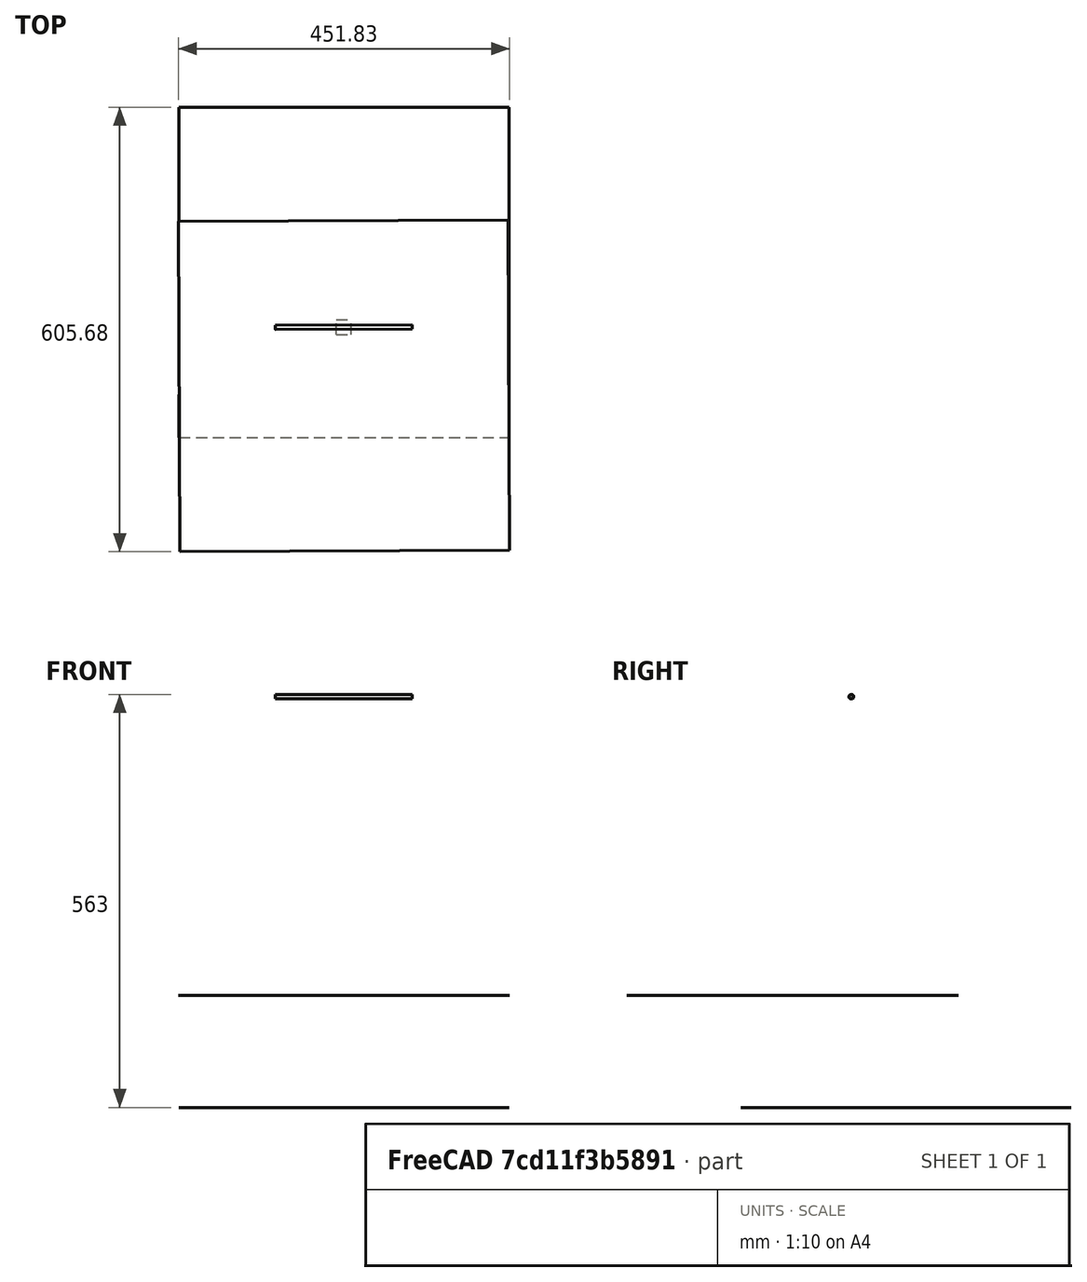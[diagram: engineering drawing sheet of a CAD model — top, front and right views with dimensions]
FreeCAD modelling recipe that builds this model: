
FCSTD DOCUMENT  (FreeCAD 0.19R18044 (Git))
Label: lift
License: Public Domain
LicenseURL: http://en.wikipedia.org/wiki/Public_domain
objects: App::FeaturePython×12, Part::FeaturePython×11, App::Link×2
note: 10 computed .brp shape members not serialized (recipe doc carries the construction recipe); baked Part::Feature solids carry a one-line shape summary decoded from their .brp
EXTERNAL_REF file=lift-middle-stage.FCStd obj=Assembly002
EXTERNAL_REF file=lift-upper-stage.FCStd obj=Assembly

FEATURE [App::Link] Link  label="lift-middle-stage"
  LinkPlacement = pos=(-0.373772,-74.7387,8.54139e-05) rot=(0,0,1;0.004077rad)
  LinkedObject = -> <external lift-middle-stage.FCStd>#Assembly002
  Placement = pos=(-0.373772,-74.7387,8.54139e-05) rot=(0,0,1;0.004077rad)
FEATURE [App::Link] Link001  label="lift-upper-stage"
  LinkPlacement = pos=(-0.0475156,-154.766,153) rot=(0,0,1;0.004077rad)
  LinkedObject = -> <external lift-upper-stage.FCStd>#Assembly
  Placement = pos=(-0.0475156,-154.766,153) rot=(0,0,1;0.004077rad)
FEATURE [Part::FeaturePython] Parts  # WARN: FeaturePython — macro-defined, semantics opaque (R4)
  Group = -> [Link,Link001,Origin]
  GroupMode = 0
FEATURE [Part::FeaturePython] Assembly  label="lift"  # WARN: FeaturePython — macro-defined, semantics opaque (R4)
  AutoRelax = true
  BuildShape = 0
  Freeze = false
  Group = -> [Constraints,Elements,Parts]
  GroupMode = 1
  SolverType = 1
  Verbose = false
  _SolverType = 1
  _Version = 1
FEATURE [App::FeaturePython] Constraints  # WARN: FeaturePython — macro-defined, semantics opaque (R4)
  Group = -> [Constraint,Constraint001,Constraint002]
  GroupMode = 1
  _Version = 1
FEATURE [App::FeaturePython] Elements  # WARN: FeaturePython — macro-defined, semantics opaque (R4)
  Group = -> [_Element,_Element001,_Element002,_Element003,_Element004,_Element005,_Element006,_Element007,_Element008]
  GroupMode = 1
FEATURE [App::FeaturePython] Constraint  label="MultiParallel"  # WARN: FeaturePython — macro-defined, semantics opaque (R4)
  Angle = 0
  AnglePitch = 0
  AngleRoll = 0
  ConstraintType = 6
  Disabled = false
  Group = -> [ElementLink,ElementLink001,ElementLink002]
  GroupMode = 1
  LockAngle = false
  _ConstraintType = 291
  _Parent = -> Constraints
FEATURE [App::FeaturePython] ElementLink  label="_Element"  # link proxy (typed FeaturePython)
  LinkTransform = true
  LinkedObject = -> _Element
  _Parent = -> Constraint
FEATURE [Part::FeaturePython] _Element  # link proxy (typed FeaturePython)
  Detach = false
  LinkTransform = true
  LinkedObject = -> Link [1.$_Element026.]
  _Parent = -> Elements
FEATURE [App::FeaturePython] ElementLink001  label="_Element001"  # link proxy (typed FeaturePython)
  LinkTransform = true
  LinkedObject = -> _Element001
  _Parent = -> Constraint
FEATURE [Part::FeaturePython] _Element001  # link proxy (typed FeaturePython)
  Detach = false
  LinkTransform = true
  LinkedObject = -> Link001 [1.$_Element024.]
  _Parent = -> Elements
FEATURE [App::FeaturePython] ElementLink002  label="_Element002"  # link proxy (typed FeaturePython)
  LinkTransform = true
  LinkedObject = -> _Element002
  _Parent = -> Constraint
FEATURE [Part::FeaturePython] _Element002  # link proxy (typed FeaturePython)
  Detach = false
  LinkTransform = true
  LinkedObject = -> Origin [XY_Plane.]
  _Parent = -> Elements
FEATURE [App::FeaturePython] Constraint001  label="AxialAlignment"  # WARN: FeaturePython — macro-defined, semantics opaque (R4)
  Angle = 0
  AnglePitch = 0
  AngleRoll = 0
  ConstraintType = 4
  Disabled = false
  Group = -> [ElementLink003,ElementLink004]
  GroupMode = 1
  LockAngle = false
  Multiply = false
  _ConstraintType = 36
  _Parent = -> Constraints
FEATURE [App::FeaturePython] ElementLink003  label="_Element003"  # link proxy (typed FeaturePython)
  LinkTransform = true
  LinkedObject = -> _Element003
  _Parent = -> Constraint001
FEATURE [Part::FeaturePython] _Element003  # link proxy (typed FeaturePython)
  Detach = false
  LinkTransform = true
  LinkedObject = -> Link001 [1.$Element.]
  _Parent = -> Elements
FEATURE [App::FeaturePython] ElementLink004  label="_Element004"  # link proxy (typed FeaturePython)
  LinkTransform = true
  LinkedObject = -> _Element004
  _Parent = -> Constraint001
FEATURE [Part::FeaturePython] _Element004  # link proxy (typed FeaturePython)
  Detach = false
  LinkTransform = true
  LinkedObject = -> Link [1.$Element002.]
  _Parent = -> Elements
FEATURE [Part::FeaturePython] _Element005  # link proxy (typed FeaturePython)
  Detach = false
  LinkTransform = true
  LinkedObject = -> Link001 [1.$Element001.]
  _Parent = -> Elements
FEATURE [Part::FeaturePython] _Element006  # link proxy (typed FeaturePython)
  Detach = false
  LinkTransform = true
  LinkedObject = -> Link [1.$_Element.]
  _Parent = -> Elements
FEATURE [Part::FeaturePython] _Element007  # link proxy (typed FeaturePython)
  Detach = false
  LinkTransform = true
  LinkedObject = -> Link [1.$Element003.]
  _Parent = -> Elements
FEATURE [Part::FeaturePython] _Element008  # link proxy (typed FeaturePython)
  Detach = false
  LinkTransform = true
  LinkedObject = -> Link [1.$Element004.]
  _Parent = -> Elements
FEATURE [App::FeaturePython] Constraint002  label="AxialAlignment001"  # WARN: FeaturePython — macro-defined, semantics opaque (R4)
  Angle = 0
  AnglePitch = 0
  AngleRoll = 0
  ConstraintType = 4
  Disabled = false
  Group = -> [ElementLink005,ElementLink006]
  GroupMode = 1
  LockAngle = false
  Multiply = false
  _ConstraintType = 36
  _Parent = -> Constraints
FEATURE [App::FeaturePython] ElementLink005  label="_Element007"  # link proxy (typed FeaturePython)
  LinkTransform = true
  LinkedObject = -> _Element007
  _Parent = -> Constraint002
FEATURE [App::FeaturePython] ElementLink006  label="_Element005"  # link proxy (typed FeaturePython)
  LinkTransform = true
  LinkedObject = -> _Element005
  _Parent = -> Constraint002

RESOLVED EXTERNAL PARTS (link-assembly join: the EXTERNAL_REF files above that resolve inside this repo's crawl, each included once):
---- part lift-middle-stage.FCStd = doc fcstd_024ec45ee0a4 ----
FCSTD DOCUMENT  (FreeCAD 0.19R18044 (Git))
Label: lift-middle-stage
License: Public Domain
LicenseURL: http://en.wikipedia.org/wiki/Public_domain
objects: App::FeaturePython×44, Part::FeaturePython×34, App::Link×6, App::LinkElement×4
note: 33 computed .brp shape members not serialized (recipe doc carries the construction recipe); baked Part::Feature solids carry a one-line shape summary decoded from their .brp
EXTERNAL_REF file=../parts/lift/middle-stage-actuator-rod.FCStd obj=Assembly
EXTERNAL_REF file=../parts/lift/middle-stage-beam.FCStd obj=Assembly001
EXTERNAL_REF file=../parts/lift/middle-stage-beam.FCStd obj=Assembly
EXTERNAL_REF file=../parts/common/linear-actuator-400.FCStd obj=Assembly004
EXTERNAL_REF file=../parts/common/rail-450.FCStd obj=Assembly002
EXTERNAL_REF file=../parts/common/rail-450.FCStd obj=Assembly

FEATURE [App::Link] Link  label="middle-stage-actuator-rod"
  LinkPlacement = pos=(0,-6.67572e-05,560) rot=(0,0,1;0rad)
  LinkedObject = -> <external ../parts/lift/middle-stage-actuator-rod.FCStd>#Assembly
  Placement = pos=(0,-6.67572e-05,560) rot=(0,0,1;0rad)
FEATURE [App::Link] Link001  label="middle-stage-beam-left"
  LinkPlacement = pos=(71.3,-24.5001,10.0001) rot=(0,0,1;0rad)
  LinkedObject = -> <external ../parts/lift/middle-stage-beam.FCStd>#Assembly001
  Placement = pos=(71.3,-24.5001,10.0001) rot=(0,0,1;0rad)
FEATURE [App::Link] Link002  label="middle-stage-beam-right"
  LinkPlacement = pos=(49.7,-24.5001,10.0001) rot=(0,0,1;0rad)
  LinkedObject = -> <external ../parts/lift/middle-stage-beam.FCStd>#Assembly
  Placement = pos=(49.7,-24.5001,10.0001) rot=(0,0,1;0rad)
FEATURE [App::Link] Link003  label="actuator_a"
  LinkPlacement = pos=(7.1213e-12,-6.67572e-05,44.0001) rot=(0,0,1;3.14159rad)
  LinkedObject = -> <external ../parts/common/linear-actuator-400.FCStd>#Assembly004
  Placement = pos=(7.1213e-12,-6.67572e-05,44.0001) rot=(0,0,1;3.14159rad)
FEATURE [App::LinkElement] Link004_i0  label="left"
  LinkPlacement = pos=(106,-6.67572e-05,565) rot=(0.57735,-0.57735,-0.57735;2.0944rad)
  LinkedObject = -> <external ../parts/common/rail-450.FCStd>#Assembly002
  Placement = pos=(106,-6.67572e-05,565) rot=(0.57735,-0.57735,-0.57735;2.0944rad)
FEATURE [App::LinkElement] Link004_i1  label="right"
  LinkPlacement = pos=(-106,-6.67572e-05,565) rot=(0.57735,0.57735,0.57735;2.0944rad)
  LinkedObject = -> <external ../parts/common/rail-450.FCStd>#Assembly002
  Placement = pos=(-106,-6.67572e-05,565) rot=(0.57735,0.57735,0.57735;2.0944rad)
FEATURE [App::Link] Link004  label="rail top"
  ElementCount = 2
  ElementList = -> [Link004_i0,Link004_i1]
  LinkedObject = -> <external ../parts/common/rail-450.FCStd>#Assembly002
FEATURE [App::LinkElement] Link005_i0  label="rail-upper-left"
  LinkPlacement = pos=(93.3,-49.0001,610) rot=(0.57735,0.57735,0.57735;2.0944rad)
  LinkedObject = -> <external ../parts/common/rail-450.FCStd>#Assembly
  Placement = pos=(93.3,-49.0001,610) rot=(0.57735,0.57735,0.57735;2.0944rad)
FEATURE [App::LinkElement] Link005_i1  label="rail-upper-right"
  LinkPlacement = pos=(-93.3,-49.0001,610) rot=(0.57735,-0.57735,-0.57735;2.0944rad)
  LinkedObject = -> <external ../parts/common/rail-450.FCStd>#Assembly
  Placement = pos=(-93.3,-49.0001,610) rot=(0.57735,-0.57735,-0.57735;2.0944rad)
FEATURE [App::Link] Link005  label="rail bottom"
  ElementCount = 2
  ElementList = -> [Link005_i0,Link005_i1]
  LinkedObject = -> <external ../parts/common/rail-450.FCStd>#Assembly
FEATURE [Part::FeaturePython] Parts002  label="Parts"  # WARN: FeaturePython — macro-defined, semantics opaque (R4)
  Group = -> [Origin004,Link,Link001,Link002,Link003,Link004,Link005]
  GroupMode = 0
FEATURE [Part::FeaturePython] Assembly002  label="lift-middle-stage"  # WARN: FeaturePython — macro-defined, semantics opaque (R4)
  AutoRelax = true
  BuildShape = 0
  Freeze = false
  Group = -> [Constraints002,Elements002,Parts002]
  GroupMode = 1
  SolverType = 1
  Verbose = false
  _SolverType = 1
  _Version = 1
FEATURE [App::FeaturePython] Constraints002  # WARN: FeaturePython — macro-defined, semantics opaque (R4)
  Group = -> [Constraint,Constraint003,Constraint004,Constraint005,Constraint006,Constraint007,Constraint008,Constraint009,Constraint010,Constraint011,Constraint012,Constraint013,Constraint014,Constraint015]
  GroupMode = 1
  _Version = 1
FEATURE [App::FeaturePython] Elements002  label="Elements"  # WARN: FeaturePython — macro-defined, semantics opaque (R4)
  Group = -> [_Element,_Element001,_Element002,_Element003,_Element004,_Element005,_Element006,_Element007,_Element008,_Element009,_Element010,_Element011,_Element012,_Element013,_Element014,_Element015,_Element016,_Element017,_Element018,_Element019,_Element020,_Element021,_Element022,_Element023,_Element024,Element,Element001,_Element025,_Element026,Element002,Element003,Element004]
  GroupMode = 1
FEATURE [App::FeaturePython] Constraint  label="Locked"  # WARN: FeaturePython — macro-defined, semantics opaque (R4)
  ConstraintType = 0
  Disabled = false
  Group = -> [ElementLink]
  GroupMode = 1
  _ConstraintType = 0
  _Parent = -> Constraints002
FEATURE [App::FeaturePython] ElementLink  label="_Element"  # link proxy (typed FeaturePython)
  LinkTransform = true
  LinkedObject = -> _Element
  _Parent = -> Constraint
FEATURE [Part::FeaturePython] _Element  # link proxy (typed FeaturePython)
  Detach = false
  LinkTransform = true
  LinkedObject = -> Link [1.$Element003.]
  _Parent = -> Elements002
FEATURE [Part::FeaturePython] _Element001  # link proxy (typed FeaturePython)
  Detach = false
  LinkTransform = true
  LinkedObject = -> Link001 [1.$actuator-rod-hole.]
  _Parent = -> Elements002
FEATURE [Part::FeaturePython] _Element002  # link proxy (typed FeaturePython)
  Detach = false
  LinkTransform = true
  LinkedObject = -> Link [1.$left.]
  _Parent = -> Elements002
FEATURE [Part::FeaturePython] _Element003  # link proxy (typed FeaturePython)
  Detach = false
  LinkTransform = true
  LinkedObject = -> Link002 [1.$actuator_rod_hole.]
  _Parent = -> Elements002
FEATURE [Part::FeaturePython] _Element004  # link proxy (typed FeaturePython)
  Detach = false
  LinkTransform = true
  LinkedObject = -> Link [1.$right.]
  _Parent = -> Elements002
FEATURE [App::FeaturePython] Constraint003  label="PlaneCoincident002"  # WARN: FeaturePython — macro-defined, semantics opaque (R4)
  Angle = 0
  AnglePitch = 0
  AngleRoll = 0
  Cascade = false
  ConstraintType = 2
  Disabled = false
  Group = -> [ElementLink005,ElementLink006]
  GroupMode = 1
  LockAngle = false
  Multiply = false
  OffsetX = 0
  OffsetY = 0
  _ConstraintType = 35
  _Parent = -> Constraints002
FEATURE [App::FeaturePython] ElementLink005  label="_Element005"  # link proxy (typed FeaturePython)
  LinkTransform = true
  LinkedObject = -> _Element005
  _Parent = -> Constraint003
FEATURE [Part::FeaturePython] _Element005  # link proxy (typed FeaturePython)
  Detach = false
  LinkTransform = true
  LinkedObject = -> Link [1.$center.]
  _Parent = -> Elements002
FEATURE [App::FeaturePython] ElementLink006  label="_Element006"  # link proxy (typed FeaturePython)
  LinkTransform = true
  LinkedObject = -> _Element006
  _Parent = -> Constraint003
FEATURE [Part::FeaturePython] _Element006  # link proxy (typed FeaturePython)
  Detach = false
  LinkTransform = true
  LinkedObject = -> Link003 [1.$mount_top.]
  _Parent = -> Elements002
FEATURE [App::FeaturePython] Constraint004  label="PlaneCoincident003"  # WARN: FeaturePython — macro-defined, semantics opaque (R4)
  Angle = 0
  AnglePitch = 0
  AngleRoll = 0
  Cascade = false
  ConstraintType = 2
  Disabled = false
  Group = -> [ElementLink007,ElementLink008]
  GroupMode = 1
  LockAngle = false
  Multiply = false
  Offset = 1
  OffsetX = 0
  OffsetY = 0
  _ConstraintType = 35
  _Parent = -> Constraints002
FEATURE [App::FeaturePython] ElementLink007  label="_Element007"  # link proxy (typed FeaturePython)
  LinkTransform = true
  LinkedObject = -> _Element007
  _Parent = -> Constraint004
FEATURE [Part::FeaturePython] _Element007  # link proxy (typed FeaturePython)
  Detach = false
  LinkTransform = true
  LinkedObject = -> Link005 [Link005_i0.1.$mount_top.]
  _Parent = -> Elements002
FEATURE [App::FeaturePython] ElementLink008  label="_Element008"  # link proxy (typed FeaturePython)
  LinkTransform = true
  LinkedObject = -> _Element008
  _Parent = -> Constraint004
FEATURE [Part::FeaturePython] _Element008  # link proxy (typed FeaturePython)
  Detach = false
  LinkTransform = true
  LinkedObject = -> Link001 [1.$rail_upper_top.]
  _Parent = -> Elements002
FEATURE [App::FeaturePython] Constraint005  label="PlaneCoincident004"  # WARN: FeaturePython — macro-defined, semantics opaque (R4)
  Angle = 0
  AnglePitch = 0
  AngleRoll = 0
  Cascade = false
  ConstraintType = 2
  Disabled = false
  Group = -> [ElementLink009,ElementLink010]
  GroupMode = 1
  LockAngle = false
  Multiply = false
  Offset = 1
  OffsetX = 0
  OffsetY = 0
  _ConstraintType = 35
  _Parent = -> Constraints002
FEATURE [App::FeaturePython] ElementLink009  label="_Element009"  # link proxy (typed FeaturePython)
  LinkTransform = true
  LinkedObject = -> _Element009
  _Parent = -> Constraint005
FEATURE [Part::FeaturePython] _Element009  # link proxy (typed FeaturePython)
  Detach = false
  LinkTransform = true
  LinkedObject = -> Link001 [1.$rail_upper_bottom.]
  _Parent = -> Elements002
FEATURE [App::FeaturePython] ElementLink010  label="_Element010"  # link proxy (typed FeaturePython)
  LinkTransform = true
  LinkedObject = -> _Element010
  _Parent = -> Constraint005
FEATURE [Part::FeaturePython] _Element010  # link proxy (typed FeaturePython)
  Detach = false
  LinkTransform = true
  LinkedObject = -> Link005 [Link005_i0.1.$mount_bottom.]
  _Parent = -> Elements002
FEATURE [App::FeaturePython] Constraint006  label="PlaneCoincident005"  # WARN: FeaturePython — macro-defined, semantics opaque (R4)
  Angle = 0
  AnglePitch = 0
  AngleRoll = 0
  Cascade = false
  ConstraintType = 2
  Disabled = false
  Group = -> [ElementLink011,ElementLink012]
  GroupMode = 1
  LockAngle = false
  Multiply = false
  Offset = -1
  OffsetX = 0
  OffsetY = 0
  _ConstraintType = 35
  _Parent = -> Constraints002
FEATURE [App::FeaturePython] ElementLink011  label="_Element011"  # link proxy (typed FeaturePython)
  LinkTransform = true
  LinkedObject = -> _Element011
  _Parent = -> Constraint006
FEATURE [Part::FeaturePython] _Element011  # link proxy (typed FeaturePython)
  Detach = false
  LinkTransform = true
  LinkedObject = -> Link005 [Link005_i1.1.$mount_top.]
  _Parent = -> Elements002
FEATURE [App::FeaturePython] ElementLink012  label="_Element012"  # link proxy (typed FeaturePython)
  LinkTransform = true
  LinkedObject = -> _Element012
  _Parent = -> Constraint006
FEATURE [Part::FeaturePython] _Element012  # link proxy (typed FeaturePython)
  Detach = false
  LinkTransform = true
  LinkedObject = -> Link002 [1.$rail_upper_top.]
  _Parent = -> Elements002
FEATURE [App::FeaturePython] Constraint007  label="PlaneCoincident006"  # WARN: FeaturePython — macro-defined, semantics opaque (R4)
  Angle = 0
  AnglePitch = 0
  AngleRoll = 0
  Cascade = false
  ConstraintType = 2
  Disabled = false
  Group = -> [ElementLink013,ElementLink014]
  GroupMode = 1
  LockAngle = false
  Multiply = false
  Offset = -1
  OffsetX = 0
  OffsetY = 0
  _ConstraintType = 35
  _Parent = -> Constraints002
FEATURE [App::FeaturePython] ElementLink013  label="_Element013"  # link proxy (typed FeaturePython)
  LinkTransform = true
  LinkedObject = -> _Element013
  _Parent = -> Constraint007
FEATURE [Part::FeaturePython] _Element013  # link proxy (typed FeaturePython)
  Detach = false
  LinkTransform = true
  LinkedObject = -> Link002 [1.$rail_upper_bottom.]
  _Parent = -> Elements002
FEATURE [App::FeaturePython] ElementLink014  label="_Element014"  # link proxy (typed FeaturePython)
  LinkTransform = true
  LinkedObject = -> _Element014
  _Parent = -> Constraint007
FEATURE [Part::FeaturePython] _Element014  # link proxy (typed FeaturePython)
  Detach = false
  LinkTransform = true
  LinkedObject = -> Link005 [Link005_i1.1.$mount_bottom.]
  _Parent = -> Elements002
FEATURE [App::FeaturePython] Constraint008  label="PlaneCoincident007"  # WARN: FeaturePython — macro-defined, semantics opaque (R4)
  Angle = 0
  AnglePitch = 0
  AngleRoll = 0
  Cascade = false
  ConstraintType = 2
  Disabled = false
  Group = -> [ElementLink015,ElementLink016]
  GroupMode = 1
  LockAngle = false
  Multiply = false
  OffsetX = 0
  OffsetY = 0
  _ConstraintType = 35
  _Parent = -> Constraints002
FEATURE [App::FeaturePython] ElementLink015  label="_Element015"  # link proxy (typed FeaturePython)
  LinkTransform = true
  LinkedObject = -> _Element015
  _Parent = -> Constraint008
FEATURE [Part::FeaturePython] _Element015  # link proxy (typed FeaturePython)
  Detach = false
  LinkTransform = true
  LinkedObject = -> Link001 [1.$rail_middle_top.]
  _Parent = -> Elements002
FEATURE [App::FeaturePython] ElementLink016  label="_Element016"  # link proxy (typed FeaturePython)
  LinkTransform = true
  LinkedObject = -> _Element016
  _Parent = -> Constraint008
FEATURE [Part::FeaturePython] _Element016  # link proxy (typed FeaturePython)
  Detach = false
  LinkTransform = true
  LinkedObject = -> Link004 [Link004_i0.1.$mount_top.]
  _Parent = -> Elements002
FEATURE [Part::FeaturePython] _Element017  # link proxy (typed FeaturePython)
  Detach = false
  LinkTransform = true
  LinkedObject = -> Link001 [1.$rail_middle_bottom.]
  _Parent = -> Elements002
FEATURE [Part::FeaturePython] _Element018  # link proxy (typed FeaturePython)
  Detach = false
  LinkTransform = true
  LinkedObject = -> Link004 [Link004_i0.1.$mount_bottom.]
  _Parent = -> Elements002
FEATURE [App::FeaturePython] Constraint009  label="PlaneCoincident008"  # WARN: FeaturePython — macro-defined, semantics opaque (R4)
  Angle = 0
  AnglePitch = 0
  AngleRoll = 0
  Cascade = false
  ConstraintType = 2
  Disabled = false
  Group = -> [ElementLink017,ElementLink018]
  GroupMode = 1
  LockAngle = false
  Multiply = false
  OffsetX = 0
  OffsetY = 0
  _ConstraintType = 35
  _Parent = -> Constraints002
FEATURE [App::FeaturePython] ElementLink017  label="_Element019"  # link proxy (typed FeaturePython)
  LinkTransform = true
  LinkedObject = -> _Element019
  _Parent = -> Constraint009
FEATURE [Part::FeaturePython] _Element019  # link proxy (typed FeaturePython)
  Detach = false
  LinkTransform = true
  LinkedObject = -> Link001 [1.$rail_middle_middle.]
  _Parent = -> Elements002
FEATURE [App::FeaturePython] ElementLink018  label="_Element020"  # link proxy (typed FeaturePython)
  LinkTransform = true
  LinkedObject = -> _Element020
  _Parent = -> Constraint009
FEATURE [Part::FeaturePython] _Element020  # link proxy (typed FeaturePython)
  Detach = false
  LinkTransform = true
  LinkedObject = -> Link004 [Link004_i0.1.$mount_middle.]
  _Parent = -> Elements002
FEATURE [App::FeaturePython] Constraint010  label="PlaneCoincident"  # WARN: FeaturePython — macro-defined, semantics opaque (R4)
  Angle = 0
  AnglePitch = 0
  AngleRoll = 0
  Cascade = false
  ConstraintType = 2
  Disabled = false
  Group = -> [ElementLink019,ElementLink020]
  GroupMode = 1
  LockAngle = false
  Multiply = false
  OffsetX = 0
  OffsetY = 0
  _ConstraintType = 35
  _Parent = -> Constraints002
FEATURE [App::FeaturePython] ElementLink019  label="_Element004"  # link proxy (typed FeaturePython)
  LinkTransform = true
  LinkedObject = -> _Element004
  _Parent = -> Constraint010
FEATURE [App::FeaturePython] ElementLink020  label="_Element001"  # link proxy (typed FeaturePython)
  LinkTransform = true
  LinkedObject = -> _Element001
  _Parent = -> Constraint010
FEATURE [App::FeaturePython] Constraint011  label="PlaneCoincident009"  # WARN: FeaturePython — macro-defined, semantics opaque (R4)
  Angle = 0
  AnglePitch = 0
  AngleRoll = 0
  Cascade = false
  ConstraintType = 2
  Disabled = false
  Group = -> [ElementLink021,ElementLink022]
  GroupMode = 1
  LockAngle = false
  Multiply = false
  OffsetX = 0
  OffsetY = 0
  _ConstraintType = 35
  _Parent = -> Constraints002
FEATURE [App::FeaturePython] ElementLink021  label="_Element002"  # link proxy (typed FeaturePython)
  LinkTransform = true
  LinkedObject = -> _Element002
  _Parent = -> Constraint011
FEATURE [App::FeaturePython] ElementLink022  label="_Element003"  # link proxy (typed FeaturePython)
  LinkTransform = true
  LinkedObject = -> _Element003
  _Parent = -> Constraint011
FEATURE [App::FeaturePython] Constraint012  label="PlaneCoincident010"  # WARN: FeaturePython — macro-defined, semantics opaque (R4)
  Angle = 0
  AnglePitch = 0
  AngleRoll = 0
  Cascade = false
  ConstraintType = 2
  Disabled = false
  Group = -> [ElementLink023,ElementLink024]
  GroupMode = 1
  LockAngle = false
  Multiply = false
  OffsetX = 0
  OffsetY = 0
  _ConstraintType = 35
  _Parent = -> Constraints002
FEATURE [App::FeaturePython] ElementLink023  label="_Element021"  # link proxy (typed FeaturePython)
  LinkTransform = true
  LinkedObject = -> _Element021
  _Parent = -> Constraint012
FEATURE [Part::FeaturePython] _Element021  # link proxy (typed FeaturePython)
  Detach = false
  LinkTransform = true
  LinkedObject = -> Link002 [1.$rail_middle_top.]
  _Parent = -> Elements002
FEATURE [App::FeaturePython] ElementLink024  label="_Element022"  # link proxy (typed FeaturePython)
  LinkTransform = true
  LinkedObject = -> _Element022
  _Parent = -> Constraint012
FEATURE [Part::FeaturePython] _Element022  # link proxy (typed FeaturePython)
  Detach = false
  LinkTransform = true
  LinkedObject = -> Link004 [Link004_i1.1.$mount_top.]
  _Parent = -> Elements002
FEATURE [App::FeaturePython] Constraint013  label="PlaneCoincident011"  # WARN: FeaturePython — macro-defined, semantics opaque (R4)
  Angle = 0
  AnglePitch = 0
  AngleRoll = 0
  Cascade = false
  ConstraintType = 2
  Disabled = false
  Group = -> [ElementLink025,ElementLink026]
  GroupMode = 1
  LockAngle = false
  Multiply = false
  OffsetX = 0
  OffsetY = 0
  _ConstraintType = 35
  _Parent = -> Constraints002
FEATURE [App::FeaturePython] ElementLink025  label="_Element023"  # link proxy (typed FeaturePython)
  LinkTransform = true
  LinkedObject = -> _Element023
  _Parent = -> Constraint013
FEATURE [Part::FeaturePython] _Element023  # link proxy (typed FeaturePython)
  Detach = false
  LinkTransform = true
  LinkedObject = -> Link002 [1.$rail_middle_middle.]
  _Parent = -> Elements002
FEATURE [App::FeaturePython] ElementLink026  label="_Element024"  # link proxy (typed FeaturePython)
  LinkTransform = true
  LinkedObject = -> _Element024
  _Parent = -> Constraint013
FEATURE [Part::FeaturePython] _Element024  # link proxy (typed FeaturePython)
  Detach = false
  LinkTransform = true
  LinkedObject = -> Link004 [Link004_i1.1.$mount_middle.]
  _Parent = -> Elements002
FEATURE [Part::FeaturePython] Element  # link proxy (typed FeaturePython)
  Detach = false
  LinkTransform = true
  LinkedObject = -> Link001 [1.$base_mount_rear.]
  _Parent = -> Elements002
FEATURE [Part::FeaturePython] Element001  # link proxy (typed FeaturePython)
  Detach = false
  LinkTransform = true
  LinkedObject = -> Link002 [1.$base_mount_rear.]
  _Parent = -> Elements002
FEATURE [App::FeaturePython] Constraint014  label="MultiParallel"  # WARN: FeaturePython — macro-defined, semantics opaque (R4)
  Angle = 0
  AnglePitch = 0
  AngleRoll = 0
  ConstraintType = 6
  Disabled = false
  Group = -> [ElementLink027,ElementLink028,ElementLink029]
  GroupMode = 1
  LockAngle = false
  _ConstraintType = 291
  _Parent = -> Constraints002
FEATURE [App::FeaturePython] ElementLink027  label="Element001"  # link proxy (typed FeaturePython)
  LinkTransform = true
  LinkedObject = -> Element001
  _Parent = -> Constraint014
FEATURE [App::FeaturePython] ElementLink028  label="Element"  # link proxy (typed FeaturePython)
  LinkTransform = true
  LinkedObject = -> Element
  _Parent = -> Constraint014
FEATURE [App::FeaturePython] ElementLink029  label="_Element025"  # link proxy (typed FeaturePython)
  LinkTransform = true
  LinkedObject = -> _Element025
  _Parent = -> Constraint014
FEATURE [Part::FeaturePython] _Element025  # link proxy (typed FeaturePython)
  Detach = false
  LinkTransform = true
  LinkedObject = -> Link003 [1.$_Element.]
  _Parent = -> Elements002
FEATURE [App::FeaturePython] Constraint015  label="MultiParallel001"  # WARN: FeaturePython — macro-defined, semantics opaque (R4)
  Angle = 0
  AnglePitch = 0
  AngleRoll = 0
  ConstraintType = 6
  Disabled = false
  Group = -> [ElementLink030,ElementLink031]
  GroupMode = 1
  LockAngle = false
  _ConstraintType = 291
  _Parent = -> Constraints002
FEATURE [App::FeaturePython] ElementLink030  label="_Element026"  # link proxy (typed FeaturePython)
  LinkTransform = true
  LinkedObject = -> _Element026
  _Parent = -> Constraint015
FEATURE [Part::FeaturePython] _Element026  # link proxy (typed FeaturePython)
  Detach = false
  LinkTransform = true
  LinkedObject = -> Origin004 [XY_Plane004.]
  _Parent = -> Elements002
FEATURE [App::FeaturePython] ElementLink031  label="Element"  # link proxy (typed FeaturePython)
  LinkTransform = true
  LinkedObject = -> Element
  _Parent = -> Constraint015
FEATURE [Part::FeaturePython] Element002  # link proxy (typed FeaturePython)
  Detach = false
  LinkTransform = true
  LinkedObject = -> Link005 [Link005_i1.1.$slide_axis.]
  _Parent = -> Elements002
FEATURE [Part::FeaturePython] Element003  # link proxy (typed FeaturePython)
  Detach = false
  LinkTransform = true
  LinkedObject = -> Link005 [Link005_i0.1.$slide_axis.]
  _Parent = -> Elements002
FEATURE [Part::FeaturePython] Element004  # link proxy (typed FeaturePython)
  Detach = false
  LinkTransform = true
  LinkedObject = -> Link004 [Link004_i1.1.$slide_axis.]
  _Parent = -> Elements002
---- part lift-upper-stage.FCStd = doc fcstd_1cc9415303b1 ----
FCSTD DOCUMENT  (FreeCAD 0.19R18044 (Git))
Label: lift-upper-stage
License: Public Domain
LicenseURL: http://en.wikipedia.org/wiki/Public_domain
objects: App::FeaturePython×40, Part::FeaturePython×29, App::Link×6, App::LinkElement×4
note: 28 computed .brp shape members not serialized (recipe doc carries the construction recipe); baked Part::Feature solids carry a one-line shape summary decoded from their .brp
EXTERNAL_REF file=../parts/lift/upper-stage-actuator-rod.FCStd obj=Assembly
EXTERNAL_REF file=../parts/lift/upper-stage-beam.FCStd obj=Assembly
EXTERNAL_REF file=../parts/lift/upper-stage-beam.FCStd obj=Assembly001
EXTERNAL_REF file=../parts/lift/upper-stage-rod.FCStd obj=Assembly
EXTERNAL_REF file=../parts/common/linear-actuator-400.FCStd obj=Assembly004
EXTERNAL_REF file=../parts/common/rail-450.FCStd obj=Assembly002

FEATURE [App::Link] Link  label="upper-stage-actuator-rod"
  LinkPlacement = pos=(9.94618e-10,3.77807,437.103) rot=(-1,0,0;4.45001rad)
  LinkedObject = -> <external ../parts/lift/upper-stage-actuator-rod.FCStd>#Assembly
  Placement = pos=(9.94618e-10,3.77807,437.103) rot=(-1,0,0;4.45001rad)
FEATURE [App::Link] Link001  label="upper-stage-beam-left"
  LinkPlacement = pos=(-128,6.52807,7.10273) rot=(0,0,1;0rad)
  LinkedObject = -> <external ../parts/lift/upper-stage-beam.FCStd>#Assembly
  Placement = pos=(-128,6.52807,7.10273) rot=(0,0,1;0rad)
FEATURE [App::Link] Link002  label="upper-stage-beam-right"
  LinkPlacement = pos=(-118,6.52807,7.10273) rot=(0,0,1;0rad)
  LinkedObject = -> <external ../parts/lift/upper-stage-beam.FCStd>#Assembly001
  Placement = pos=(-118,6.52807,7.10273) rot=(0,0,1;0rad)
FEATURE [App::Link] Link004  label="actuator_a"
  LinkPlacement = pos=(9.25419e-08,3.77807,-78.8973) rot=(0,0,1;0rad)
  LinkedObject = -> <external ../parts/common/linear-actuator-400.FCStd>#Assembly004
  Placement = pos=(9.25419e-08,3.77807,-78.8973) rot=(0,0,1;0rad)
FEATURE [App::LinkElement] Link003_i0  label="top"
  LinkPlacement = pos=(3.02068e-10,-20.4719,357.103) rot=(0,0,1;0rad)
  LinkedObject = -> <external ../parts/lift/upper-stage-rod.FCStd>#Assembly
  Placement = pos=(3.02068e-10,-20.4719,357.103) rot=(0,0,1;0rad)
FEATURE [App::LinkElement] Link003_i1  label="bottom"
  LinkPlacement = pos=(7.62902e-11,-20.4719,227.103) rot=(0,0,1;0rad)
  LinkedObject = -> <external ../parts/lift/upper-stage-rod.FCStd>#Assembly
  Placement = pos=(7.62902e-11,-20.4719,227.103) rot=(0,0,1;0rad)
FEATURE [App::Link] Link003  label="upper-stage-rod"
  ElementCount = 2
  ElementList = -> [Link003_i0,Link003_i1]
  LinkedObject = -> <external ../parts/lift/upper-stage-rod.FCStd>#Assembly
FEATURE [App::LinkElement] Link005_i0  label="rail left"
  LinkPlacement = pos=(-93.3,31.0281,457.103) rot=(0.57735,-0.57735,-0.57735;2.0944rad)
  LinkedObject = -> <external ../parts/common/rail-450.FCStd>#Assembly002
  Placement = pos=(-93.3,31.0281,457.103) rot=(0.57735,-0.57735,-0.57735;2.0944rad)
FEATURE [App::LinkElement] Link005_i1  label="rail right"
  LinkPlacement = pos=(93.3,31.0281,457.103) rot=(0.57735,0.57735,0.57735;2.0944rad)
  LinkedObject = -> <external ../parts/common/rail-450.FCStd>#Assembly002
  Placement = pos=(93.3,31.0281,457.103) rot=(0.57735,0.57735,0.57735;2.0944rad)
FEATURE [App::Link] Link005  label="rail top"
  ElementCount = 2
  ElementList = -> [Link005_i0,Link005_i1]
  LinkedObject = -> <external ../parts/common/rail-450.FCStd>#Assembly002
FEATURE [Part::FeaturePython] Parts  # WARN: FeaturePython — macro-defined, semantics opaque (R4)
  Group = -> [Link,Link001,Link002,Link003,Link004,Origin,Link005]
  GroupMode = 0
FEATURE [Part::FeaturePython] Assembly  label="lift-upper-stage"  # WARN: FeaturePython — macro-defined, semantics opaque (R4)
  AutoRelax = true
  BuildShape = 0
  Freeze = false
  Group = -> [Constraints,Elements,Parts]
  GroupMode = 1
  SolverType = 1
  Verbose = false
  _SolverType = 1
  _Version = 1
FEATURE [App::FeaturePython] Constraints  # WARN: FeaturePython — macro-defined, semantics opaque (R4)
  Group = -> [Constraint,Constraint001,Constraint002,Constraint003,Constraint004,Constraint005,Constraint006,Constraint007,Constraint008,Constraint009,Constraint010,Constraint011,Constraint012]
  GroupMode = 1
  _Version = 1
FEATURE [App::FeaturePython] Elements  # WARN: FeaturePython — macro-defined, semantics opaque (R4)
  Group = -> [_Element,_Element001,_Element002,_Element003,_Element004,_Element005,_Element006,_Element007,_Element008,_Element009,_Element010,_Element011,_Element012,_Element013,_Element015,_Element016,_Element017,_Element018,_Element019,_Element020,_Element021,_Element022,_Element023,_Element024,_Element025,Element,Element001]
  GroupMode = 1
FEATURE [App::FeaturePython] Constraint  label="Locked"  # WARN: FeaturePython — macro-defined, semantics opaque (R4)
  ConstraintType = 0
  Disabled = false
  Group = -> [ElementLink]
  GroupMode = 1
  _ConstraintType = 0
  _Parent = -> Constraints
FEATURE [App::FeaturePython] ElementLink  label="_Element"  # link proxy (typed FeaturePython)
  LinkTransform = true
  LinkedObject = -> _Element
  _Parent = -> Constraint
FEATURE [Part::FeaturePython] _Element  # link proxy (typed FeaturePython)
  Detach = false
  LinkTransform = true
  LinkedObject = -> Link [1.$Element003.]
  _Parent = -> Elements
FEATURE [Part::FeaturePython] _Element001  # link proxy (typed FeaturePython)
  Detach = false
  LinkTransform = true
  LinkedObject = -> Link [1.$left.]
  _Parent = -> Elements
FEATURE [Part::FeaturePython] _Element002  # link proxy (typed FeaturePython)
  Detach = false
  LinkTransform = true
  LinkedObject = -> Link001 [1.$actuator_rod_hole.]
  _Parent = -> Elements
FEATURE [App::FeaturePython] Constraint001  label="PlaneCoincident"  # WARN: FeaturePython — macro-defined, semantics opaque (R4)
  Angle = 0
  AnglePitch = 0
  AngleRoll = 0
  Cascade = false
  ConstraintType = 2
  Disabled = false
  Group = -> [ElementLink001,ElementLink002]
  GroupMode = 1
  LockAngle = false
  Multiply = false
  Offset = -44
  OffsetX = 0
  OffsetY = 0
  _ConstraintType = 35
  _Parent = -> Constraints
FEATURE [App::FeaturePython] ElementLink001  label="_Element001"  # link proxy (typed FeaturePython)
  LinkTransform = true
  LinkedObject = -> _Element001
  _Parent = -> Constraint001
FEATURE [App::FeaturePython] ElementLink002  label="_Element002"  # link proxy (typed FeaturePython)
  LinkTransform = true
  LinkedObject = -> _Element002
  _Parent = -> Constraint001
FEATURE [App::FeaturePython] Constraint002  label="PlaneCoincident001"  # WARN: FeaturePython — macro-defined, semantics opaque (R4)
  Angle = 0
  AnglePitch = 0
  AngleRoll = 0
  Cascade = false
  ConstraintType = 2
  Disabled = false
  Group = -> [ElementLink003,ElementLink004]
  GroupMode = 1
  LockAngle = false
  Multiply = false
  Offset = -44
  OffsetX = 0
  OffsetY = 0
  _ConstraintType = 35
  _Parent = -> Constraints
FEATURE [App::FeaturePython] ElementLink003  label="_Element003"  # link proxy (typed FeaturePython)
  LinkTransform = true
  LinkedObject = -> _Element003
  _Parent = -> Constraint002
FEATURE [Part::FeaturePython] _Element003  # link proxy (typed FeaturePython)
  Detach = false
  LinkTransform = true
  LinkedObject = -> Link002 [1.$actuator_rod_hole.]
  _Parent = -> Elements
FEATURE [App::FeaturePython] ElementLink004  label="_Element004"  # link proxy (typed FeaturePython)
  LinkTransform = true
  LinkedObject = -> _Element004
  _Parent = -> Constraint002
FEATURE [Part::FeaturePython] _Element004  # link proxy (typed FeaturePython)
  Detach = false
  LinkTransform = true
  LinkedObject = -> Link [1.$right.]
  _Parent = -> Elements
FEATURE [App::FeaturePython] Constraint003  label="AxialAlignment"  # WARN: FeaturePython — macro-defined, semantics opaque (R4)
  Angle = 0
  AnglePitch = 0
  AngleRoll = 0
  ConstraintType = 4
  Disabled = false
  Group = -> [ElementLink005,ElementLink006]
  GroupMode = 1
  LockAngle = false
  Multiply = false
  _ConstraintType = 36
  _Parent = -> Constraints
FEATURE [App::FeaturePython] ElementLink005  label="_Element005"  # link proxy (typed FeaturePython)
  LinkTransform = true
  LinkedObject = -> _Element005
  _Parent = -> Constraint003
FEATURE [Part::FeaturePython] _Element005  # link proxy (typed FeaturePython)
  Detach = false
  LinkTransform = true
  LinkedObject = -> Link [1.$middle.]
  _Parent = -> Elements
FEATURE [App::FeaturePython] ElementLink006  label="_Element006"  # link proxy (typed FeaturePython)
  LinkTransform = true
  LinkedObject = -> _Element006
  _Parent = -> Constraint003
FEATURE [Part::FeaturePython] _Element006  # link proxy (typed FeaturePython)
  Detach = false
  LinkTransform = true
  LinkedObject = -> Link004 [1.$mount_top.]
  _Parent = -> Elements
FEATURE [App::FeaturePython] Constraint004  label="PlaneCoincident002"  # WARN: FeaturePython — macro-defined, semantics opaque (R4)
  Angle = 0
  AnglePitch = 0
  AngleRoll = 0
  Cascade = false
  ConstraintType = 2
  Disabled = false
  Group = -> [ElementLink007,ElementLink008]
  GroupMode = 1
  LockAngle = false
  Multiply = false
  Offset = -119
  OffsetX = 0
  OffsetY = 0
  _ConstraintType = 35
  _Parent = -> Constraints
FEATURE [App::FeaturePython] ElementLink007  label="_Element007"  # link proxy (typed FeaturePython)
  LinkTransform = true
  LinkedObject = -> _Element007
  _Parent = -> Constraint004
FEATURE [Part::FeaturePython] _Element007  # link proxy (typed FeaturePython)
  Detach = false
  LinkTransform = true
  LinkedObject = -> Link003 [Link003_i0.1.$left.]
  _Parent = -> Elements
FEATURE [App::FeaturePython] ElementLink008  label="_Element008"  # link proxy (typed FeaturePython)
  LinkTransform = true
  LinkedObject = -> _Element008
  _Parent = -> Constraint004
FEATURE [Part::FeaturePython] _Element008  # link proxy (typed FeaturePython)
  Detach = false
  LinkTransform = true
  LinkedObject = -> Link001 [1.$tv_rod_hole_top.]
  _Parent = -> Elements
FEATURE [App::FeaturePython] Constraint005  label="PlaneCoincident003"  # WARN: FeaturePython — macro-defined, semantics opaque (R4)
  Angle = 0
  AnglePitch = 0
  AngleRoll = 0
  Cascade = false
  ConstraintType = 2
  Disabled = false
  Group = -> [ElementLink009,ElementLink010]
  GroupMode = 1
  LockAngle = false
  Multiply = false
  Offset = 119
  OffsetX = 0
  OffsetY = 0
  _ConstraintType = 35
  _Parent = -> Constraints
FEATURE [App::FeaturePython] ElementLink009  label="_Element009"  # link proxy (typed FeaturePython)
  LinkTransform = true
  LinkedObject = -> _Element009
  _Parent = -> Constraint005
FEATURE [Part::FeaturePython] _Element009  # link proxy (typed FeaturePython)
  Detach = false
  LinkTransform = true
  LinkedObject = -> Link001 [1.$tv_rod_hole_bottom.]
  _Parent = -> Elements
FEATURE [App::FeaturePython] ElementLink010  label="_Element010"  # link proxy (typed FeaturePython)
  LinkTransform = true
  LinkedObject = -> _Element010
  _Parent = -> Constraint005
FEATURE [Part::FeaturePython] _Element010  # link proxy (typed FeaturePython)
  Detach = false
  LinkTransform = true
  LinkedObject = -> Link003 [Link003_i1.1.$left.]
  _Parent = -> Elements
FEATURE [Part::FeaturePython] _Element011  # link proxy (typed FeaturePython)
  Detach = false
  LinkTransform = true
  LinkedObject = -> Link002 [1.$tv_rod_hole_top.]
  _Parent = -> Elements
FEATURE [Part::FeaturePython] _Element012  # link proxy (typed FeaturePython)
  Detach = false
  LinkTransform = true
  LinkedObject = -> Link003 [Link003_i0.1.$right.]
  _Parent = -> Elements
FEATURE [App::FeaturePython] Constraint006  label="AxialAlignment001"  # WARN: FeaturePython — macro-defined, semantics opaque (R4)
  Angle = 0
  AnglePitch = 0
  AngleRoll = 0
  ConstraintType = 4
  Disabled = false
  Group = -> [ElementLink011,ElementLink012]
  GroupMode = 1
  LockAngle = false
  Multiply = false
  _ConstraintType = 36
  _Parent = -> Constraints
FEATURE [App::FeaturePython] ElementLink011  label="_Element011"  # link proxy (typed FeaturePython)
  LinkTransform = true
  LinkedObject = -> _Element011
  _Parent = -> Constraint006
FEATURE [App::FeaturePython] ElementLink012  label="_Element012"  # link proxy (typed FeaturePython)
  LinkTransform = true
  LinkedObject = -> _Element012
  _Parent = -> Constraint006
FEATURE [Part::FeaturePython] _Element013  # link proxy (typed FeaturePython)
  Detach = false
  LinkTransform = true
  LinkedObject = -> Link001 [1.$base_edge.]
  _Parent = -> Elements
FEATURE [Part::FeaturePython] _Element015  # link proxy (typed FeaturePython)
  Detach = false
  LinkTransform = true
  LinkedObject = -> Origin [Y_Axis.]
  _Parent = -> Elements
FEATURE [App::FeaturePython] Constraint007  label="MultiParallel"  # WARN: FeaturePython — macro-defined, semantics opaque (R4)
  Angle = 0
  AnglePitch = 0
  AngleRoll = 0
  ConstraintType = 6
  Disabled = false
  Group = -> [ElementLink013,ElementLink014]
  GroupMode = 1
  LockAngle = false
  _ConstraintType = 291
  _Parent = -> Constraints
FEATURE [App::FeaturePython] ElementLink013  label="_Element015"  # link proxy (typed FeaturePython)
  LinkTransform = true
  LinkedObject = -> _Element015
  _Parent = -> Constraint007
FEATURE [App::FeaturePython] ElementLink014  label="_Element013"  # link proxy (typed FeaturePython)
  LinkTransform = true
  LinkedObject = -> _Element013
  _Parent = -> Constraint007
FEATURE [Part::FeaturePython] _Element016  # link proxy (typed FeaturePython)
  Detach = false
  LinkTransform = true
  LinkedObject = -> Link001 [1.$rail_hole_top.]
  _Parent = -> Elements
FEATURE [Part::FeaturePython] _Element017  # link proxy (typed FeaturePython)
  Detach = false
  LinkTransform = true
  LinkedObject = -> Link005 [Link005_i0.1.$mount_top.]
  _Parent = -> Elements
FEATURE [Part::FeaturePython] _Element018  # link proxy (typed FeaturePython)
  Detach = false
  LinkTransform = true
  LinkedObject = -> Link001 [1.$rail-hole-middle.]
  _Parent = -> Elements
FEATURE [Part::FeaturePython] _Element019  # link proxy (typed FeaturePython)
  Detach = false
  LinkTransform = true
  LinkedObject = -> Link005 [Link005_i0.1.$mount_middle.]
  _Parent = -> Elements
FEATURE [App::FeaturePython] Constraint008  label="PlaneCoincident004"  # WARN: FeaturePython — macro-defined, semantics opaque (R4)
  Angle = 0
  AnglePitch = 0
  AngleRoll = 0
  Cascade = false
  ConstraintType = 2
  Disabled = false
  Group = -> [ElementLink015,ElementLink016]
  GroupMode = 1
  LockAngle = false
  Multiply = false
  OffsetX = 0
  OffsetY = 0
  _ConstraintType = 35
  _Parent = -> Constraints
FEATURE [App::FeaturePython] ElementLink015  label="_Element016"  # link proxy (typed FeaturePython)
  LinkTransform = true
  LinkedObject = -> _Element016
  _Parent = -> Constraint008
FEATURE [App::FeaturePython] ElementLink016  label="_Element017"  # link proxy (typed FeaturePython)
  LinkTransform = true
  LinkedObject = -> _Element017
  _Parent = -> Constraint008
FEATURE [App::FeaturePython] Constraint009  label="PlaneCoincident005"  # WARN: FeaturePython — macro-defined, semantics opaque (R4)
  Angle = 0
  AnglePitch = 0
  AngleRoll = 0
  Cascade = false
  ConstraintType = 2
  Disabled = false
  Group = -> [ElementLink017,ElementLink018]
  GroupMode = 1
  LockAngle = false
  Multiply = false
  OffsetX = 0
  OffsetY = 0
  _ConstraintType = 35
  _Parent = -> Constraints
FEATURE [App::FeaturePython] ElementLink017  label="_Element019"  # link proxy (typed FeaturePython)
  LinkTransform = true
  LinkedObject = -> _Element019
  _Parent = -> Constraint009
FEATURE [App::FeaturePython] ElementLink018  label="_Element018"  # link proxy (typed FeaturePython)
  LinkTransform = true
  LinkedObject = -> _Element018
  _Parent = -> Constraint009
FEATURE [App::FeaturePython] Constraint010  label="PlaneCoincident006"  # WARN: FeaturePython — macro-defined, semantics opaque (R4)
  Angle = 0
  AnglePitch = 0
  AngleRoll = 0
  Cascade = false
  ConstraintType = 2
  Disabled = false
  Group = -> [ElementLink019,ElementLink020]
  GroupMode = 1
  LockAngle = false
  Multiply = false
  OffsetX = 0
  OffsetY = 0
  _ConstraintType = 35
  _Parent = -> Constraints
FEATURE [App::FeaturePython] ElementLink019  label="_Element020"  # link proxy (typed FeaturePython)
  LinkTransform = true
  LinkedObject = -> _Element020
  _Parent = -> Constraint010
FEATURE [Part::FeaturePython] _Element020  # link proxy (typed FeaturePython)
  Detach = false
  LinkTransform = true
  LinkedObject = -> Link005 [Link005_i1.1.$mount_top.]
  _Parent = -> Elements
FEATURE [App::FeaturePython] ElementLink020  label="_Element021"  # link proxy (typed FeaturePython)
  LinkTransform = true
  LinkedObject = -> _Element021
  _Parent = -> Constraint010
FEATURE [Part::FeaturePython] _Element021  # link proxy (typed FeaturePython)
  Detach = false
  LinkTransform = true
  LinkedObject = -> Link002 [1.$rail_hole_top.]
  _Parent = -> Elements
FEATURE [App::FeaturePython] Constraint011  label="PlaneCoincident007"  # WARN: FeaturePython — macro-defined, semantics opaque (R4)
  Angle = 0
  AnglePitch = 0
  AngleRoll = 0
  Cascade = false
  ConstraintType = 2
  Disabled = false
  Group = -> [ElementLink021,ElementLink022]
  GroupMode = 1
  LockAngle = false
  Multiply = false
  OffsetX = 0
  OffsetY = 0
  _ConstraintType = 35
  _Parent = -> Constraints
FEATURE [App::FeaturePython] ElementLink021  label="_Element022"  # link proxy (typed FeaturePython)
  LinkTransform = true
  LinkedObject = -> _Element022
  _Parent = -> Constraint011
FEATURE [Part::FeaturePython] _Element022  # link proxy (typed FeaturePython)
  Detach = false
  LinkTransform = true
  LinkedObject = -> Link002 [1.$rail_hole_middle.]
  _Parent = -> Elements
FEATURE [App::FeaturePython] ElementLink022  label="_Element023"  # link proxy (typed FeaturePython)
  LinkTransform = true
  LinkedObject = -> _Element023
  _Parent = -> Constraint011
FEATURE [Part::FeaturePython] _Element023  # link proxy (typed FeaturePython)
  Detach = false
  LinkTransform = true
  LinkedObject = -> Link005 [Link005_i1.1.$mount_middle.]
  _Parent = -> Elements
FEATURE [App::FeaturePython] Constraint012  label="MultiParallel001"  # WARN: FeaturePython — macro-defined, semantics opaque (R4)
  Angle = 0
  AnglePitch = 0
  AngleRoll = 0
  ConstraintType = 6
  Disabled = false
  Group = -> [ElementLink023,ElementLink024]
  GroupMode = 1
  LockAngle = false
  _ConstraintType = 291
  _Parent = -> Constraints
FEATURE [App::FeaturePython] ElementLink023  label="_Element024"  # link proxy (typed FeaturePython)
  LinkTransform = true
  LinkedObject = -> _Element024
  _Parent = -> Constraint012
FEATURE [Part::FeaturePython] _Element024  # link proxy (typed FeaturePython)
  Detach = false
  LinkTransform = true
  LinkedObject = -> Origin [XY_Plane.]
  _Parent = -> Elements
FEATURE [App::FeaturePython] ElementLink024  label="_Element025"  # link proxy (typed FeaturePython)
  LinkTransform = true
  LinkedObject = -> _Element025
  _Parent = -> Constraint012
FEATURE [Part::FeaturePython] _Element025  # link proxy (typed FeaturePython)
  Detach = false
  LinkTransform = true
  LinkedObject = -> Link004 [1.$_Element.]
  _Parent = -> Elements
FEATURE [Part::FeaturePython] Element  # link proxy (typed FeaturePython)
  Detach = false
  LinkTransform = true
  LinkedObject = -> Link005 [Link005_i0.1.$slide_axis.]
  _Parent = -> Elements
FEATURE [Part::FeaturePython] Element001  # link proxy (typed FeaturePython)
  Detach = false
  LinkTransform = true
  LinkedObject = -> Link005 [Link005_i1.1.$slide_axis.]
  _Parent = -> Elements
